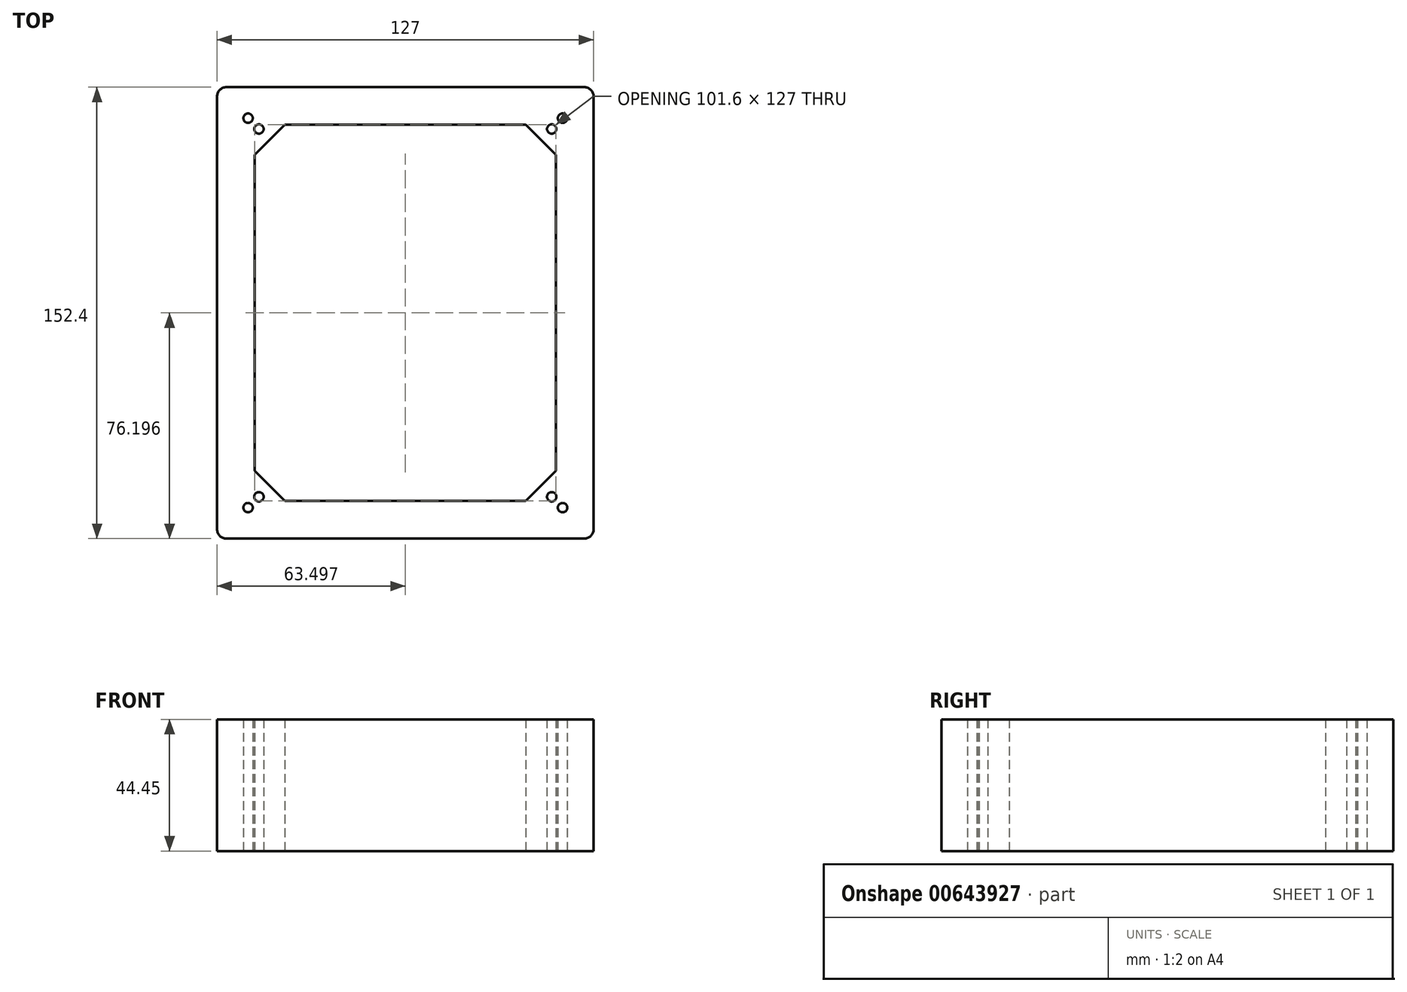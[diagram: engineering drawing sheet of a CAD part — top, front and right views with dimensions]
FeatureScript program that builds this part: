
annotation { "Feature Type Name" : "Feature", "Feature Type Description" : "" }
export const myFeature = defineFeature(function(context is Context, id is Id, definition is map)
    precondition{}
    {
        {
            var Q0;
            Q0=qCreatedBy(makeId("Top.planeOp"),FACE);
            var sketch = newSketch(context, id + "F0", { "sketchPlane" : qUnion([Q0])});
            skLineSegment(sketch, "E0.bottom", {"start": v(-60.12, 76.46) * mm, "end": v(60.53, 76.46) * mm});
            skLineSegment(sketch, "E0.top", {"start": v(-60.12, -75.94) * mm, "end": v(60.53, -75.94) * mm});
            skLineSegment(sketch, "E0.left", {"start": v(-63.3, 73.28) * mm, "end": v(-63.3, -72.77) * mm});
            skLineSegment(sketch, "E0.right", {"start": v(63.7, 73.28) * mm, "end": v(63.7, -72.77) * mm});
            skPoint(sketch, "E0.middle", {"position": v(0.2, 0.26) * mm});
            skLineSegment(sketch, "E1.bottom", {"start": v(-53.77, 70.1) * mm, "end": v(54.18, 70.1) * mm});
            skLineSegment(sketch, "E1.top", {"start": v(-53.77, -69.6) * mm, "end": v(54.18, -69.6) * mm});
            skLineSegment(sketch, "E1.left", {"start": v(-56.94, 66.93) * mm, "end": v(-56.94, -66.42) * mm});
            skLineSegment(sketch, "E1.right", {"start": v(57.36, 66.93) * mm, "end": v(57.36, -66.42) * mm});
            skLineSegment(sketch, "E2.bottom", {"start": v(-47.42, 63.76) * mm, "end": v(47.83, 63.76) * mm});
            skLineSegment(sketch, "E2.top", {"start": v(-47.42, -63.24) * mm, "end": v(48.46, -63.24) * mm});
            skLineSegment(sketch, "E2.left", {"start": v(-50.6, 60.58) * mm, "end": v(-50.6, -60.07) * mm});
            skLineSegment(sketch, "E2.right", {"start": v(51, 60.58) * mm, "end": v(51, -60.7) * mm});
            skPoint(sketch, "E3.visualSharp", {"position": v(-56.94, 70.1) * mm});
            skArc(sketch, "E3.filletArc", {"start": v(-53.77, 70.1) * mm, "mid": v(-56.01, 69.18) * mm, "end": v(-56.94, 66.93) * mm});
            skPoint(sketch, "E4.visualSharp", {"position": v(57.36, 70.1) * mm});
            skArc(sketch, "E4.filletArc", {"start": v(57.36, 66.93) * mm, "mid": v(56.43, 69.18) * mm, "end": v(54.18, 70.1) * mm});
            skPoint(sketch, "E5.visualSharp", {"position": v(57.36, -69.6) * mm});
            skArc(sketch, "E5.filletArc", {"start": v(54.18, -69.6) * mm, "mid": v(56.43, -68.66) * mm, "end": v(57.36, -66.42) * mm});
            skPoint(sketch, "E6.visualSharp", {"position": v(-56.94, -69.6) * mm});
            skArc(sketch, "E6.filletArc", {"start": v(-56.94, -66.42) * mm, "mid": v(-56.01, -68.66) * mm, "end": v(-53.77, -69.6) * mm});
            skPoint(sketch, "E7.visualSharp", {"position": v(51, 63.76) * mm});
            skArc(sketch, "E7.filletArc", {"start": v(51, 60.58) * mm, "mid": v(50.08, 62.83) * mm, "end": v(47.83, 63.76) * mm});
            skPoint(sketch, "E8.visualSharp", {"position": v(51, -63.24) * mm});
            skArc(sketch, "E8.filletArc", {"start": v(48.46, -63.24) * mm, "mid": v(50.26, -62.5) * mm, "end": v(51, -60.7) * mm});
            skPoint(sketch, "E9.visualSharp", {"position": v(-50.6, -63.24) * mm});
            skArc(sketch, "E9.filletArc", {"start": v(-50.6, -60.07) * mm, "mid": v(-49.66, -62.31) * mm, "end": v(-47.42, -63.24) * mm});
            skArc(sketch, "E10.filletArc", {"start": v(-47.42, 63.76) * mm, "mid": v(-49.66, 62.83) * mm, "end": v(-50.6, 60.58) * mm});
            skPoint(sketch, "E11.visualSharp", {"position": v(-63.3, 76.46) * mm});
            skArc(sketch, "E11.filletArc", {"start": v(-60.12, 76.46) * mm, "mid": v(-62.36, 75.53) * mm, "end": v(-63.3, 73.28) * mm});
            skPoint(sketch, "E12.visualSharp", {"position": v(63.7, 76.46) * mm});
            skArc(sketch, "E12.filletArc", {"start": v(63.7, 73.28) * mm, "mid": v(62.78, 75.53) * mm, "end": v(60.53, 76.46) * mm});
            skPoint(sketch, "E13.visualSharp", {"position": v(63.7, -75.94) * mm});
            skArc(sketch, "E13.filletArc", {"start": v(60.53, -75.94) * mm, "mid": v(62.78, -75.01) * mm, "end": v(63.7, -72.77) * mm});
            skPoint(sketch, "E14.visualSharp", {"position": v(-63.3, -75.94) * mm});
            skArc(sketch, "E14.filletArc", {"start": v(-63.3, -72.77) * mm, "mid": v(-62.36, -75.01) * mm, "end": v(-60.12, -75.94) * mm});
            skPoint(sketch, "E15", {"position": v(16.08, 63.76) * mm});
            skPoint(sketch, "E16", {"position": v(16.08, 76.46) * mm});
            skPoint(sketch, "E17", {"position": v(16.08, -63.24) * mm});
            skPoint(sketch, "E18", {"position": v(16.08, -75.94) * mm});
            skPoint(sketch, "E19", {"position": v(-15.67, 76.46) * mm});
            skPoint(sketch, "E20", {"position": v(-15.67, 63.76) * mm});
            skPoint(sketch, "E21", {"position": v(-15.67, -63.24) * mm});
            skPoint(sketch, "E22", {"position": v(-15.67, -75.94) * mm});
            skPoint(sketch, "E23", {"position": v(0.2, 76.46) * mm});
            skPoint(sketch, "E24", {"position": v(0.2, -75.94) * mm});
            skPoint(sketch, "E25", {"position": v(-63.3, 0.26) * mm});
            skPoint(sketch, "E26", {"position": v(63.7, 0.26) * mm});
            skPoint(sketch, "E27", {"position": v(63.7, 16.13) * mm});
            skPoint(sketch, "E28", {"position": v(51, 16.13) * mm});
            skPoint(sketch, "E29", {"position": v(-50.6, 16.13) * mm});
            skPoint(sketch, "E30", {"position": v(-63.3, 16.13) * mm});
            skPoint(sketch, "E31", {"position": v(63.7, -15.62) * mm});
            skPoint(sketch, "E32", {"position": v(51, -15.62) * mm});
            skPoint(sketch, "E33", {"position": v(-50.6, -15.62) * mm});
            skPoint(sketch, "E34", {"position": v(-63.3, -15.62) * mm});
            skPoint(sketch, "E35", {"position": v(40.85, 63.76) * mm});
            skPoint(sketch, "E36", {"position": v(40.85, -63.24) * mm});
            skPoint(sketch, "E37", {"position": v(-40.43, 63.76) * mm});
            skPoint(sketch, "E38", {"position": v(-40.43, -63.24) * mm});
            skPoint(sketch, "E39", {"position": v(-50.6, -53.08) * mm});
            skPoint(sketch, "E40", {"position": v(51, -53.08) * mm});
            skPoint(sketch, "E41", {"position": v(51, 53.6) * mm});
            skPoint(sketch, "E42", {"position": v(-50.6, 53.6) * mm});
            skLineSegment(sketch, "E43", {"start": v(-50.6, 53.6) * mm, "end": v(-40.43, 63.76) * mm});
            skLineSegment(sketch, "E44", {"start": v(40.85, 63.76) * mm, "end": v(51, 53.6) * mm});
            skLineSegment(sketch, "E45", {"start": v(51, -53.08) * mm, "end": v(40.85, -63.24) * mm});
            skLineSegment(sketch, "E46", {"start": v(-40.43, -63.24) * mm, "end": v(-50.6, -53.08) * mm});
            skPoint(sketch, "E47", {"position": v(-45.51, 58.68) * mm});
            skPoint(sketch, "E48", {"position": v(45.93, 58.68) * mm});
            skPoint(sketch, "E49", {"position": v(45.93, -58.16) * mm});
            skPoint(sketch, "E50", {"position": v(-45.51, -58.16) * mm});
            skPoint(sketch, "E51", {"position": v(30.37, 76.46) * mm});
            skPoint(sketch, "E52", {"position": v(30.37, 63.76) * mm});
            skPoint(sketch, "E53", {"position": v(30.37, -63.24) * mm});
            skPoint(sketch, "E54", {"position": v(30.37, -75.94) * mm});
            skPoint(sketch, "E55", {"position": v(-29.96, 76.46) * mm});
            skPoint(sketch, "E56", {"position": v(-29.96, 63.76) * mm});
            skPoint(sketch, "E57", {"position": v(-29.96, -63.24) * mm});
            skPoint(sketch, "E58", {"position": v(-29.96, -75.94) * mm});
            skPoint(sketch, "E59", {"position": v(63.7, 36.77) * mm});
            skPoint(sketch, "E60", {"position": v(51, 36.77) * mm});
            skPoint(sketch, "E61", {"position": v(-50.6, 36.77) * mm});
            skPoint(sketch, "E62", {"position": v(-63.3, 36.77) * mm});
            skPoint(sketch, "E63", {"position": v(63.7, -36.26) * mm});
            skPoint(sketch, "E64", {"position": v(51, -36.26) * mm});
            skPoint(sketch, "E65", {"position": v(-50.6, -36.26) * mm});
            skPoint(sketch, "E66", {"position": v(-63.3, -36.26) * mm});
            skPoint(sketch, "E67", {"position": v(-36.3, 76.46) * mm});
            skPoint(sketch, "E68", {"position": v(-36.3, 63.76) * mm});
            skPoint(sketch, "E69", {"position": v(-36.3, -63.24) * mm});
            skPoint(sketch, "E70", {"position": v(-36.3, -75.94) * mm});
            skPoint(sketch, "E71", {"position": v(36.72, 76.46) * mm});
            skPoint(sketch, "E72", {"position": v(36.72, 63.76) * mm});
            skPoint(sketch, "E73", {"position": v(36.72, -63.24) * mm});
            skPoint(sketch, "E74", {"position": v(36.72, -75.94) * mm});
            skPoint(sketch, "E75", {"position": v(-23.6, 76.46) * mm});
            skPoint(sketch, "E76", {"position": v(-23.6, 63.76) * mm});
            skPoint(sketch, "E77", {"position": v(24.02, 76.46) * mm});
            skPoint(sketch, "E78", {"position": v(24.02, 63.76) * mm});
            skPoint(sketch, "E79", {"position": v(24.02, -63.24) * mm});
            skPoint(sketch, "E80", {"position": v(24.02, -75.94) * mm});
            skPoint(sketch, "E81", {"position": v(-23.6, -63.24) * mm});
            skPoint(sketch, "E82", {"position": v(-23.6, -75.94) * mm});
            skPoint(sketch, "E83", {"position": v(-63.3, 43.12) * mm});
            skPoint(sketch, "E84", {"position": v(-50.6, 43.12) * mm});
            skPoint(sketch, "E85", {"position": v(51, 43.12) * mm});
            skPoint(sketch, "E86", {"position": v(63.7, 43.12) * mm});
            skPoint(sketch, "E87", {"position": v(-63.3, 30.42) * mm});
            skPoint(sketch, "E88", {"position": v(-50.6, 30.42) * mm});
            skPoint(sketch, "E89", {"position": v(51, 30.42) * mm});
            skPoint(sketch, "E90", {"position": v(63.7, 30.42) * mm});
            skPoint(sketch, "E91", {"position": v(-63.3, -29.9) * mm});
            skPoint(sketch, "E92", {"position": v(-50.6, -29.9) * mm});
            skPoint(sketch, "E93", {"position": v(51, -29.9) * mm});
            skPoint(sketch, "E94", {"position": v(63.7, -29.9) * mm});
            skPoint(sketch, "E95", {"position": v(-63.3, -42.6) * mm});
            skPoint(sketch, "E96", {"position": v(-50.6, -42.6) * mm});
            skPoint(sketch, "E97", {"position": v(51, -42.6) * mm});
            skPoint(sketch, "E98", {"position": v(63.7, -42.6) * mm});
            skLineSegment(sketch, "E99", {"start": v(57.36, 70.1) * mm, "end": v(45.93, 58.68) * mm, "construction": true});
            skLineSegment(sketch, "E100", {"start": v(57.36, -69.6) * mm, "end": v(45.93, -58.16) * mm, "construction": true});
            skLineSegment(sketch, "E101", {"start": v(-56.94, -69.6) * mm, "end": v(-45.51, -58.16) * mm, "construction": true});
            skPoint(sketch, "E102", {"position": v(53.25, 66) * mm});
            skLineSegment(sketch, "E103", {"start": v(-56.94, 70.1) * mm, "end": v(-45.51, 58.68) * mm, "construction": true});
            skPoint(sketch, "E104", {"position": v(-52.83, 66) * mm});
            skPoint(sketch, "E105", {"position": v(53.25, -65.48) * mm});
            skPoint(sketch, "E106", {"position": v(-52.83, -65.48) * mm});
            skCircle(sketch, "E107", {"center": v(-52.83, 66) * mm, "radius": 1.59 * mm});
            skCircle(sketch, "E108", {"center": v(53.25, 66) * mm, "radius": 1.59 * mm});
            skCircle(sketch, "E109", {"center": v(53.25, -65.48) * mm, "radius": 1.59 * mm});
            skCircle(sketch, "E110", {"center": v(-52.83, -65.48) * mm, "radius": 1.59 * mm});
            skPoint(sketch, "E111", {"position": v(-49.17, -61.82) * mm});
            skPoint(sketch, "E112", {"position": v(49.58, -61.82) * mm});
            skCircle(sketch, "E113", {"center": v(-49.17, -61.82) * mm, "radius": 1.59 * mm});
            skCircle(sketch, "E114", {"center": v(49.58, -61.82) * mm, "radius": 1.59 * mm});
            skPoint(sketch, "E115", {"position": v(-49.17, 62.33) * mm});
            skPoint(sketch, "E116", {"position": v(49.58, 62.33) * mm});
            skCircle(sketch, "E117", {"center": v(-49.17, 62.33) * mm, "radius": 1.59 * mm});
            skCircle(sketch, "E118", {"center": v(49.58, 62.33) * mm, "radius": 1.59 * mm});
            skSolve(sketch);
        }
        {
            var Q0;
            Q0=makeQuery(id+"F0.imprint","IMPRINT",FACE,{"disambiguationData":[TD([[makeQuery(id+"F0.imprint","IMPRINT",EDGE,{"derivedFrom":sQuery(id+"F0.wireOp",EDGE,"E0.bottom")}),-1.0]])]});
            var Q1;
            Q1=makeQuery(id+"F0.imprint","IMPRINT",FACE,{"disambiguationData":[TD([[makeQuery(id+"F0.imprint","IMPRINT",EDGE,{"derivedFrom":sQuery(id+"F0.wireOp",EDGE,"E1.bottom")}),-1.0]])]});
            var Q2;
            {var subQ5=sQuery(id+"F0.wireOp",EDGE,"E43");Q2=makeQuery(id+"F0.imprint","IMPRINT",FACE,{"disambiguationData":[TD([[makeQuery(id+"F0.imprint","IMPRINT",EDGE,{"derivedFrom":subQ5}),1.0]])]});}
            var Q3;
            {var subQ8=sQuery(id+"F0.wireOp",EDGE,"E44");Q3=makeQuery(id+"F0.imprint","IMPRINT",FACE,{"disambiguationData":[TD([[makeQuery(id+"F0.imprint","IMPRINT",EDGE,{"derivedFrom":subQ8}),1.0]])]});}
            var Q4;
            {var subQ8=sQuery(id+"F0.wireOp",EDGE,"E45");Q4=makeQuery(id+"F0.imprint","IMPRINT",FACE,{"disambiguationData":[TD([[makeQuery(id+"F0.imprint","IMPRINT",EDGE,{"derivedFrom":subQ8}),1.0]])]});}
            var Q5;
            {var subQ5=sQuery(id+"F0.wireOp",EDGE,"E46");Q5=makeQuery(id+"F0.imprint","IMPRINT",FACE,{"disambiguationData":[TD([[makeQuery(id+"F0.imprint","IMPRINT",EDGE,{"derivedFrom":subQ5}),1.0]])]});}
            extrude(context, id + "F1", {"entities" : qUnion([Q0, Q1, Q2, Q3, Q4, Q5]), "depth" : 44.45 * mm, "offsetDistance" : 25.4 * mm});
        }
    });
